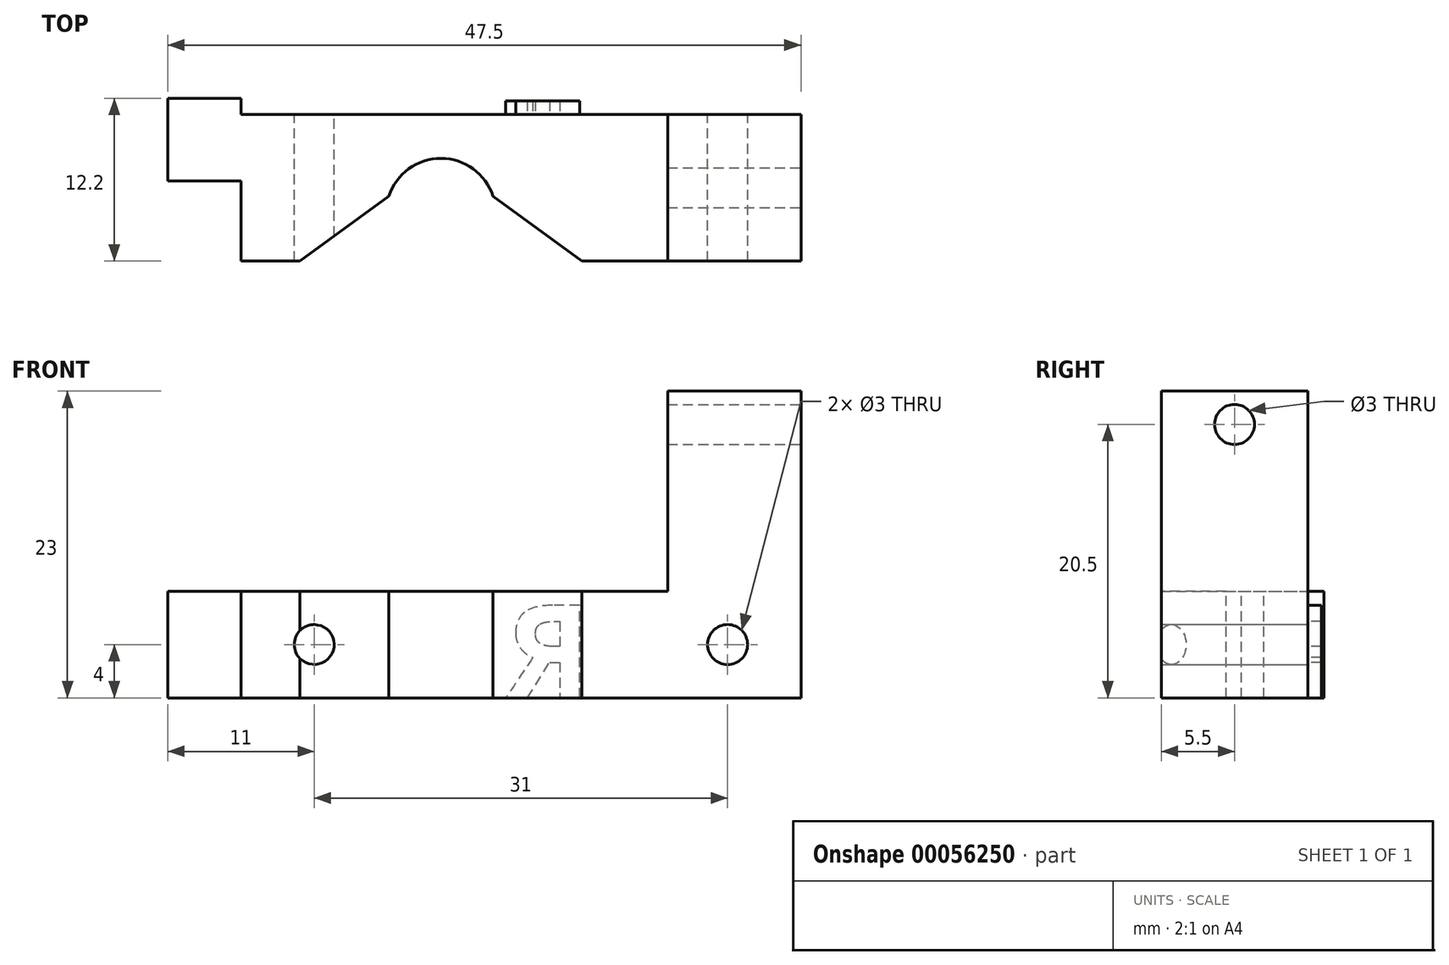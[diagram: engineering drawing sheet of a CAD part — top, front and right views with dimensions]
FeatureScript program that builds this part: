
annotation { "Feature Type Name" : "Feature", "Feature Type Description" : "" }
export const myFeature = defineFeature(function(context is Context, id is Id, definition is map)
    precondition{}
    {
        {
            assignVariable(context, id + "F0", {"name" : "rods", "anyValue" : 8});
        }
        {
            var Q0;
            Q0=qCreatedBy(makeId("Top.planeOp"),FACE);
            var sketch = newSketch(context, id + "F1", { "sketchPlane" : qUnion([Q0])});
            skLineSegment(sketch, "E0.bottom", {"start": v(0, 0) * mm, "end": v(42, 0) * mm});
            skLineSegment(sketch, "E0.top", {"start": v(0, 11) * mm, "end": v(42, 11) * mm});
            skLineSegment(sketch, "E0.left", {"start": v(0, 0) * mm, "end": v(0, 11) * mm});
            skLineSegment(sketch, "E0.right", {"start": v(42, 0) * mm, "end": v(42, 11) * mm});
            skSolve(sketch);
        }
        {
            var Q0;
            Q0=qSketchRegion(id+"F1",true);
            extrude(context, id + "F2", {"entities" : qUnion([Q0]), "depth" : 8 * mm});
        }
        {
            var Q0;
            Q0=makeQuery(id+"F2.opExtrude","CAP_FACE",FACE,{"disambiguationData":[OSD([sQuery(id+"F1.wireOp",EDGE,"E0.bottom"),sQuery(id+"F1.wireOp",EDGE,"E0.top"),sQuery(id+"F1.wireOp",EDGE,"E0.left"),sQuery(id+"F1.wireOp",EDGE,"E0.right")])],"isStart":false});
            var sketch = newSketch(context, id + "F3", { "sketchPlane" : qUnion([Q0])});
            skCircle(sketch, "E1", {"center": v(15, 3.6) * mm, "radius": 4.1 * mm});
            skSolve(sketch);
        }
        {
            var Q0;
            Q0=qSketchRegion(id+"F3",true);
            extrude(context, id + "F4", {"entities" : qUnion([Q0]), "operationType" : NewBodyOperationType.REMOVE, "oppositeDirection" : true, "depth" : 25 * mm});
        }
        {
            var Q0;
            Q0=makeQuery(id+"F4.boolean.opBoolean","INTERSECT",EDGE,{"disambiguationData":[OD(0.0)],"derivedFrom":[makeQuery(id+"F2.opExtrude","SWEPT_FACE",FACE,{"disambiguationData":[OSD([sQuery(id+"F1.wireOp",EDGE,"E0.bottom")])]}),makeQuery(id+"F4.opExtrude","SWEPT_FACE",FACE,{"disambiguationData":[OSD([sQuery(id+"F3.wireOp",EDGE,"E1")])]})]});
            var Q1;
            Q1=makeQuery(id+"F4.boolean.opBoolean","INTERSECT",EDGE,{"disambiguationData":[OD(1.0)],"derivedFrom":[makeQuery(id+"F2.opExtrude","SWEPT_FACE",FACE,{"disambiguationData":[OSD([sQuery(id+"F1.wireOp",EDGE,"E0.bottom")])]}),makeQuery(id+"F4.opExtrude","SWEPT_FACE",FACE,{"disambiguationData":[OSD([sQuery(id+"F3.wireOp",EDGE,"E1")])]})]});
            chamfer(context, id + "F5", {"entities" : qUnion([Q0, Q1]), "width" : (getVariable(context, 'rods') - 1) * mm, "tangentPropagation" : true});
        }
        {
            var Q0;
            Q0=makeQuery(id+"F2.opExtrude","SWEPT_FACE",FACE,{"disambiguationData":[OSD([sQuery(id+"F1.wireOp",EDGE,"E0.top")])]});
            var sketch = newSketch(context, id + "F6", { "sketchPlane" : qUnion([Q0])});
            skCircle(sketch, "E2", {"center": v(-5.5, 4) * mm, "radius": 1.5 * mm});
            skCircle(sketch, "E3", {"center": v(-36.5, 4) * mm, "radius": 1.5 * mm});
            skLineSegment(sketch, "E4", {"start": v(-5.5, 0) * mm, "end": v(-5.5, 8) * mm});
            skLineSegment(sketch, "E5", {"start": v(-5.5, 4) * mm, "end": v(0, 4) * mm});
            skLineSegment(sketch, "E6", {"start": v(-36.5, 4) * mm, "end": v(-42, 4) * mm});
            skSolve(sketch);
        }
        {
            var Q0;
            Q0=qSketchRegion(id+"F6",true);
            extrude(context, id + "F7", {"entities" : qUnion([Q0]), "operationType" : NewBodyOperationType.REMOVE, "oppositeDirection" : true, "depth" : 25 * mm});
        }
        {
            var Q0;
            Q0=makeQuery(id+"F2.opExtrude","SWEPT_FACE",FACE,{"disambiguationData":[OSD([sQuery(id+"F1.wireOp",EDGE,"E0.top")])]});
            var sketch = newSketch(context, id + "F8", { "sketchPlane" : qUnion([Q0])});
            skText(sketch, "E7", { "text": "R", "fontName": "OpenSans-Bold.ttf"});
            const initialGuessF8  = {"E7": [-0.02627, 0, 1, 0, 0.007]};
            skSetInitialGuess(sketch, initialGuessF8);
            skSolve(sketch);
        }
        {
            var Q0;
            Q0=qSketchRegion(id+"F8",true);
            extrude(context, id + "F9", {"entities" : qUnion([Q0]), "operationType" : NewBodyOperationType.ADD, "depth" : 1 * mm});
        }
        {
            var Q0;
            Q0=makeQuery(id+"F2.opExtrude","CAP_FACE",FACE,{"disambiguationData":[OSD([sQuery(id+"F1.wireOp",EDGE,"E0.bottom"),sQuery(id+"F1.wireOp",EDGE,"E0.top"),sQuery(id+"F1.wireOp",EDGE,"E0.left"),sQuery(id+"F1.wireOp",EDGE,"E0.right")])],"isStart":false});
            var sketch = newSketch(context, id + "F10", { "sketchPlane" : qUnion([Q0])});
            skLineSegment(sketch, "E8.bottom", {"start": v(42, 0) * mm, "end": v(32, 0) * mm});
            skLineSegment(sketch, "E8.top", {"start": v(42, 11) * mm, "end": v(32, 11) * mm});
            skLineSegment(sketch, "E8.left", {"start": v(42, 0) * mm, "end": v(42, 11) * mm});
            skLineSegment(sketch, "E8.right", {"start": v(32, 0) * mm, "end": v(32, 11) * mm});
            skSolve(sketch);
        }
        {
            var Q0;
            Q0=qSketchRegion(id+"F10",true);
            extrude(context, id + "F11", {"entities" : qUnion([Q0]), "operationType" : NewBodyOperationType.ADD, "depth" : 15 * mm});
        }
        {
            var Q0;
            Q0=makeQuery(id+"FJdLS7F1L1csLPb_1.boolean.opBoolean","MERGE",FACE,{"derivedFrom":[makeQuery(id+"F11.boolean.opBoolean","MERGE",FACE,{"derivedFrom":[makeQuery(id+"F2.opExtrude","SWEPT_FACE",FACE,{"disambiguationData":[OSD([sQuery(id+"F1.wireOp",EDGE,"E0.right")])]}),makeQuery(id+"F11.opExtrude","SWEPT_FACE",FACE,{"disambiguationData":[OSD([sQuery(id+"F10.wireOp",EDGE,"E8.left")])]})]}),makeQuery(id+"FJdLS7F1L1csLPb_1.opExtrude","SWEPT_FACE",FACE,{"disambiguationData":[OSD([sQuery(id+"F4Ds6MLMi3WL0gL_1.wireOp",EDGE,"f6963c6d-1d98-4eef-b5cd-deae189cd3ae.left")])]})]});
            var sketch = newSketch(context, id + "F12", { "sketchPlane" : qUnion([Q0])});
            skCircle(sketch, "E9", {"center": v(5.5, 20.5) * mm, "radius": 1.5 * mm});
            skPoint(sketch, "E10", {"position": v(0, 20.5) * mm});
            skPoint(sketch, "E11", {"position": v(5.5, 0) * mm});
            skSolve(sketch);
        }
        {
            var Q0;
            Q0=qSketchRegion(id+"F12",true);
            extrude(context, id + "F13", {"entities" : qUnion([Q0]), "operationType" : NewBodyOperationType.REMOVE, "oppositeDirection" : true, "depth" : 25 * mm});
        }
        {
            var Q0;
            Q0=makeQuery(id+"F2.opExtrude","SWEPT_FACE",FACE,{"disambiguationData":[OSD([sQuery(id+"F1.wireOp",EDGE,"E0.left")])]});
            var sketch = newSketch(context, id + "F14", { "sketchPlane" : qUnion([Q0])});
            skLineSegment(sketch, "E12.right", {"start": v(-12.2, 0) * mm, "end": v(-12.2, 8) * mm});
            skLineSegment(sketch, "E13", {"start": v(-12.2, 0) * mm, "end": v(-6, 0) * mm});
            skLineSegment(sketch, "E14", {"start": v(-6, 0) * mm, "end": v(-6, 8) * mm});
            skLineSegment(sketch, "E15", {"start": v(-6, 8) * mm, "end": v(-12.2, 8) * mm});
            skSolve(sketch);
        }
        {
            var Q0;
            Q0 = qSketchRegion(id + "F14", true);
            extrude(context, id + "F15", {"entities" : qUnion([Q0]), "operationType" : NewBodyOperationType.ADD, "depth" : 5.5 * mm});
        }
    });
